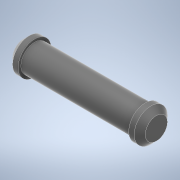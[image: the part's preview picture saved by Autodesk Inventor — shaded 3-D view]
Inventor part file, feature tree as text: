
AUTODESK INVENTOR PART (.ipt)
format: ipt  version: 2021 (Build 250183000, 183)  size: 117,248 bytes
history: native  units: mm
features: extrude x3, sketch x3, chamfer x2
ambient origin geometry x8: Origin, YZ Plane, XZ Plane, XY Plane, X Axis, Y Axis, Z Axis, Center Point
bodies: Solid1 (feature_tree)
feature tree (8):
  extrude  "Extrusion1"  Depth=20.0mm TaperAngle=0.0deg
  extrude  "Extrusion2"  Depth=2.0mm TaperAngle=0.0deg
  chamfer  "Chamfer1"  Distance=2.0mm Angle=45.0deg
  extrude  "Extrusion3"  Depth=2.0mm TaperAngle=45.0deg
  chamfer  "Chamfer2"  [1 undecoded]
  sketch  "Sketch1"  dims[d0=5.0mm d1=20.0mm d2=0.0mm]
  sketch  "Sketch2"  dims[d3=6.0mm d4=2.0mm d5=0.0mm d6=1.0mm d7=2.0mm d8=45.0deg]
  sketch  "Sketch3"  dims[d9=2.0mm d10=0.0mm d11=1.0mm d12=2.0mm d13=45.0deg]
note: 1 required parameter value undecoded (feature->parameter linkage not recoverable at this tier; creation-order binding heuristic only, values carry confidence <= 0.55)
